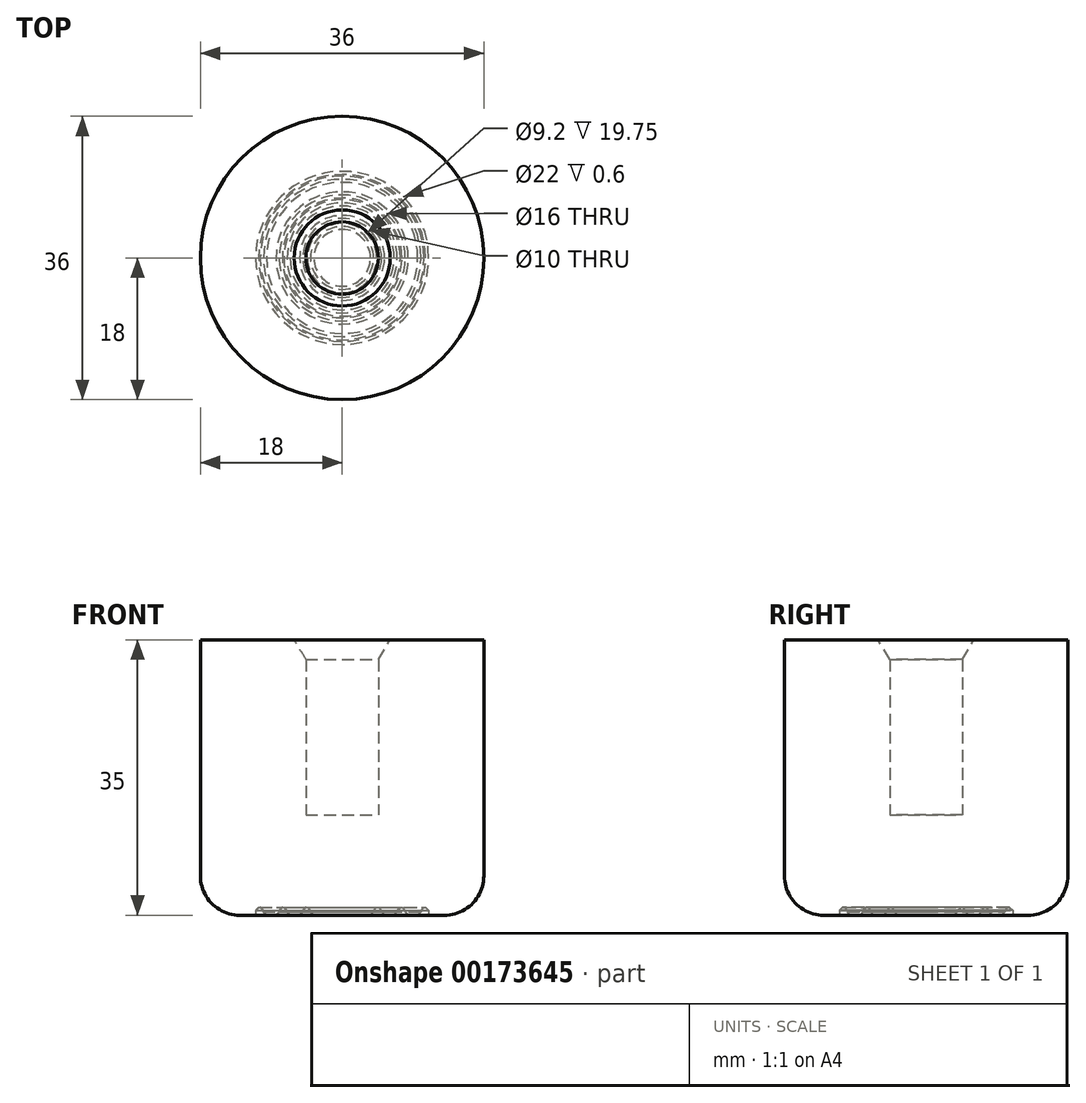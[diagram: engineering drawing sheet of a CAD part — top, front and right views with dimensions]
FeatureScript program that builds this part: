
annotation { "Feature Type Name" : "Feature", "Feature Type Description" : "" }
export const myFeature = defineFeature(function(context is Context, id is Id, definition is map)
    precondition{}
    {
        {
            var Q0;
            Q0=qCreatedBy(makeId("Front.planeOp"),FACE);
            var sketch = newSketch(context, id + "F0", { "sketchPlane" : qUnion([Q0])});
            skLineSegment(sketch, "E0", {"start": v(0, 0) * mm, "end": v(13, 0) * mm});
            skLineSegment(sketch, "E1", {"start": v(0, 0) * mm, "end": v(0, 48.67) * mm, "construction": true});
            skLineSegment(sketch, "E2", {"start": v(18, 5) * mm, "end": v(18, 35) * mm});
            skLineSegment(sketch, "E3", {"start": v(18, 35) * mm, "end": v(4.6, 35) * mm});
            skLineSegment(sketch, "E4", {"start": v(4.6, 35) * mm, "end": v(4.6, 12.75) * mm});
            skLineSegment(sketch, "E5", {"start": v(4.6, 12.75) * mm, "end": v(0, 12.75) * mm});
            skPoint(sketch, "E6.visualSharp", {"position": v(18, 0) * mm});
            skArc(sketch, "E6.filletArc", {"start": v(13, 0) * mm, "mid": v(16.54, 1.46) * mm, "end": v(18, 5) * mm});
            skLineSegment(sketch, "E7", {"start": v(4.6, 32.5) * mm, "end": v(6.1, 35) * mm});
            skLineSegment(sketch, "E8", {"start": v(0, 0) * mm, "end": v(0, 12.75) * mm});
            skSolve(sketch);
        }
        {
            var Q0;
            Q0=makeQuery(id+"F0.imprint","IMPRINT",FACE,{"disambiguationData":[TD([[makeQuery(id+"F0.imprint","IMPRINT",EDGE,{"derivedFrom":sQuery(id+"F0.wireOp",EDGE,"E0")}),1.0]])]});
            var Q1;
            Q1=sQuery(id+"F0.wireOp",EDGE,"E1");
            revolve(context, id + "F1", {"entities" : qUnion([Q0]), "axis" : qUnion([Q1]), "revolveType" : RevolveType.FULL});
        }
        {
            var Q0;
            Q0=makeQuery(id+"F1.opRevolve","SWEPT_FACE",FACE,{"disambiguationData":[OSD([sQuery(id+"F0.wireOp",EDGE,"E0")])]});
            var sketch = newSketch(context, id + "F2", { "sketchPlane" : qUnion([Q0])});
            skCircle(sketch, "E9", {"center": v(0, 0) * mm, "radius": 11 * mm});
            skCircle(sketch, "E10", {"center": v(0, 0) * mm, "radius": 10 * mm});
            skCircle(sketch, "E11", {"center": v(0, 0) * mm, "radius": 8 * mm});
            skCircle(sketch, "E12", {"center": v(0, 0) * mm, "radius": 7 * mm});
            skCircle(sketch, "E13", {"center": v(0, 0) * mm, "radius": 5 * mm});
            skCircle(sketch, "E14", {"center": v(0, 0) * mm, "radius": 4 * mm});
            skSolve(sketch);
        }
        {
            var Q0;
            Q0=makeQuery(id+"F2.imprint","IMPRINT",FACE,{"disambiguationData":[TD([[makeQuery(id+"F2.imprint","IMPRINT",EDGE,{"derivedFrom":sQuery(id+"F2.wireOp",EDGE,"E9")}),1.0]])]});
            var Q1;
            Q1=makeQuery(id+"F2.imprint","IMPRINT",FACE,{"disambiguationData":[TD([[makeQuery(id+"F2.imprint","IMPRINT",EDGE,{"derivedFrom":sQuery(id+"F2.wireOp",EDGE,"E11")}),1.0]])]});
            var Q2;
            Q2=makeQuery(id+"F2.imprint","IMPRINT",FACE,{"disambiguationData":[TD([[makeQuery(id+"F2.imprint","IMPRINT",EDGE,{"derivedFrom":sQuery(id+"F2.wireOp",EDGE,"E13")}),1.0]])]});
            extrude(context, id + "F3", {"entities" : qUnion([Q0, Q1, Q2]), "operationType" : NewBodyOperationType.REMOVE, "oppositeDirection" : true, "depth" : 1 * mm});
        }
        {
            var Q0;
            Q0=makeQuery(id+"F3.boolean.opBoolean","COPY",EDGE,{"derivedFrom":makeQuery(id+"F3.opExtrude","CAP_EDGE",EDGE,{"disambiguationData":[OSD([sQuery(id+"F2.wireOp",EDGE,"E9")])],"isStart":true})});
            var Q1;
            Q1=makeQuery(id+"F3.boolean.opBoolean","COPY",EDGE,{"derivedFrom":makeQuery(id+"F3.opExtrude","CAP_EDGE",EDGE,{"disambiguationData":[OSD([sQuery(id+"F2.wireOp",EDGE,"E10")])],"isStart":true})});
            var Q2;
            Q2=makeQuery(id+"F3.boolean.opBoolean","COPY",EDGE,{"derivedFrom":makeQuery(id+"F3.opExtrude","CAP_EDGE",EDGE,{"disambiguationData":[OSD([sQuery(id+"F2.wireOp",EDGE,"E11")])],"isStart":true})});
            var Q3;
            Q3=makeQuery(id+"F3.boolean.opBoolean","COPY",EDGE,{"derivedFrom":makeQuery(id+"F3.opExtrude","CAP_EDGE",EDGE,{"disambiguationData":[OSD([sQuery(id+"F2.wireOp",EDGE,"E12")])],"isStart":true})});
            var Q4;
            Q4=makeQuery(id+"F3.boolean.opBoolean","COPY",EDGE,{"derivedFrom":makeQuery(id+"F3.opExtrude","CAP_EDGE",EDGE,{"disambiguationData":[OSD([sQuery(id+"F2.wireOp",EDGE,"E13")])],"isStart":true})});
            var Q5;
            Q5=makeQuery(id+"F3.boolean.opBoolean","COPY",EDGE,{"derivedFrom":makeQuery(id+"F3.opExtrude","CAP_EDGE",EDGE,{"disambiguationData":[OSD([sQuery(id+"F2.wireOp",EDGE,"E14")])],"isStart":true})});
            chamfer(context, id + "F4", {"entities" : qUnion([Q0, Q1, Q2, Q3, Q4, Q5]), "width" : .4 * mm, "tangentPropagation" : true});
        }
        {
            var Q0;
            Q0=makeQuery(id+"F3.boolean.opBoolean","COPY",EDGE,{"derivedFrom":makeQuery(id+"F3.opExtrude","CAP_EDGE",EDGE,{"disambiguationData":[OSD([sQuery(id+"F2.wireOp",EDGE,"E9")])],"isStart":false})});
            var Q1;
            Q1=makeQuery(id+"F3.boolean.opBoolean","COPY",EDGE,{"derivedFrom":makeQuery(id+"F3.opExtrude","CAP_EDGE",EDGE,{"disambiguationData":[OSD([sQuery(id+"F2.wireOp",EDGE,"E10")])],"isStart":false})});
            var Q2;
            Q2=makeQuery(id+"F3.boolean.opBoolean","COPY",EDGE,{"derivedFrom":makeQuery(id+"F3.opExtrude","CAP_EDGE",EDGE,{"disambiguationData":[OSD([sQuery(id+"F2.wireOp",EDGE,"E11")])],"isStart":false})});
            var Q3;
            Q3=makeQuery(id+"F3.boolean.opBoolean","COPY",EDGE,{"derivedFrom":makeQuery(id+"F3.opExtrude","CAP_EDGE",EDGE,{"disambiguationData":[OSD([sQuery(id+"F2.wireOp",EDGE,"E12")])],"isStart":false})});
            var Q4;
            Q4=makeQuery(id+"F3.boolean.opBoolean","COPY",EDGE,{"derivedFrom":makeQuery(id+"F3.opExtrude","CAP_EDGE",EDGE,{"disambiguationData":[OSD([sQuery(id+"F2.wireOp",EDGE,"E13")])],"isStart":false})});
            var Q5;
            Q5=makeQuery(id+"F3.boolean.opBoolean","COPY",EDGE,{"derivedFrom":makeQuery(id+"F3.opExtrude","CAP_EDGE",EDGE,{"disambiguationData":[OSD([sQuery(id+"F2.wireOp",EDGE,"E14")])],"isStart":false})});
            chamfer(context, id + "F5", {"entities" : qUnion([Q0, Q1, Q2, Q3, Q4, Q5]), "width" : .4 * mm, "tangentPropagation" : true});
        }
    });
